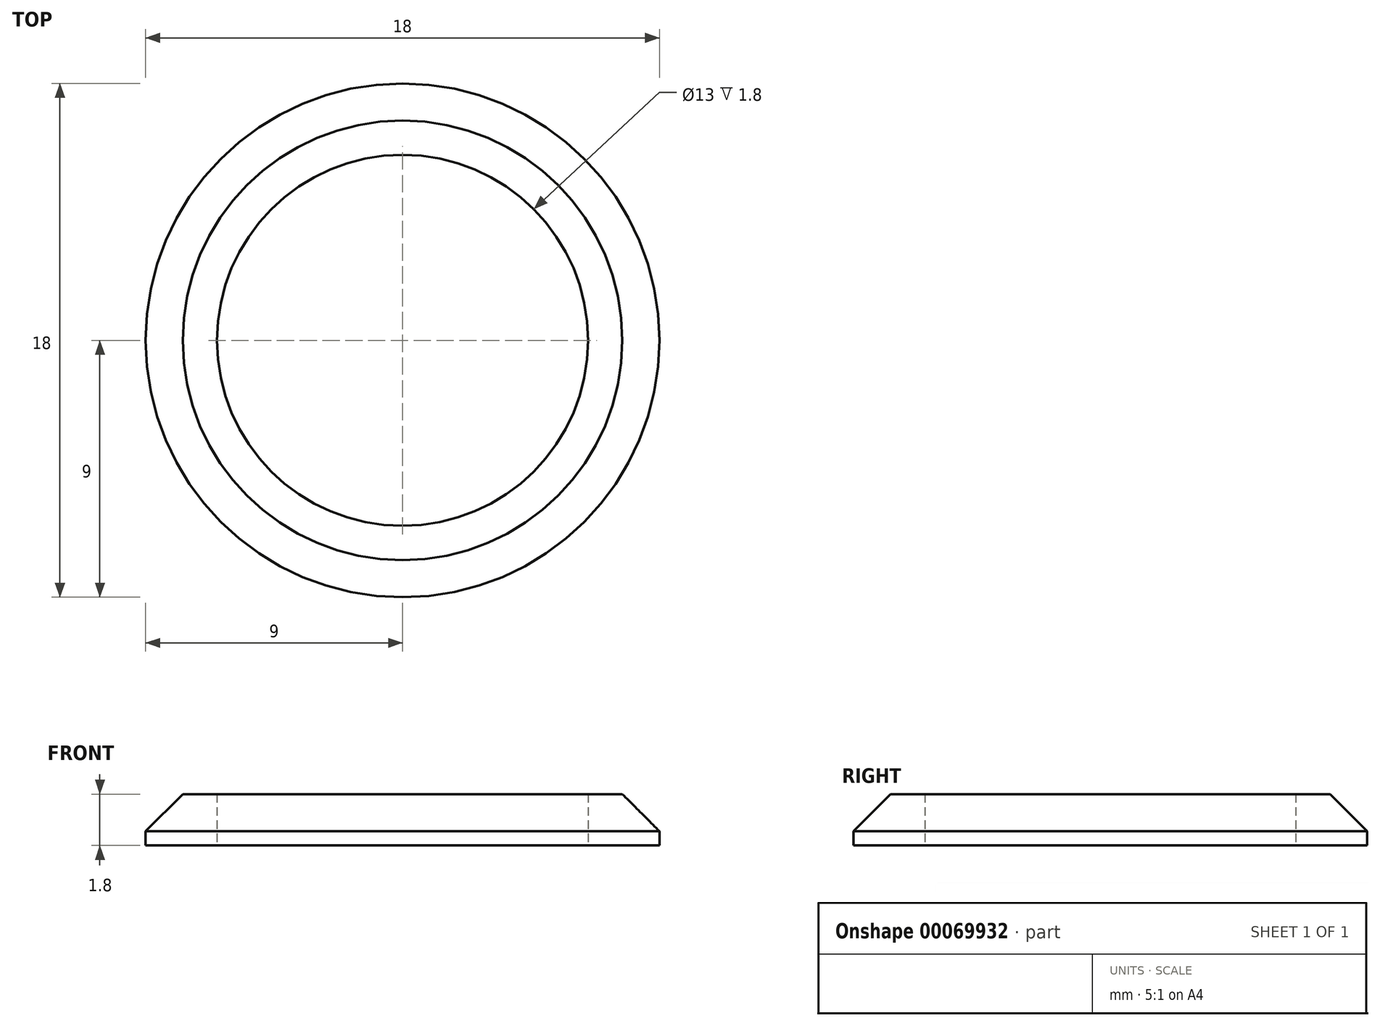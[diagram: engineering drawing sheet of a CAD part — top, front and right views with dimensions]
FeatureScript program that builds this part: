
annotation { "Feature Type Name" : "Feature", "Feature Type Description" : "" }
export const myFeature = defineFeature(function(context is Context, id is Id, definition is map)
    precondition{}
    {
        {
            var Q0;
            Q0=qCreatedBy(makeId("Top.planeOp"),FACE);
            var sketch = newSketch(context, id + "F0", { "sketchPlane" : qUnion([Q0])});
            skCircle(sketch, "E0", {"center": v(0, 0) * mm, "radius": 6.5 * mm});
            skCircle(sketch, "E1", {"center": v(0, 0) * mm, "radius": 9 * mm});
            skSolve(sketch);
        }
        {
            var Q0;
            Q0=makeQuery(id+"F0.imprint","IMPRINT",FACE,{"disambiguationData":[TD([[makeQuery(id+"F0.imprint","IMPRINT",EDGE,{"derivedFrom":sQuery(id+"F0.wireOp",EDGE,"E0")}),-1.0]])]});
            extrude(context, id + "F1", {"entities" : qUnion([Q0]), "depth" : 1.8 * mm});
        }
        {
            var Q0;
            Q0=makeQuery(id+"F1.opExtrude","CAP_EDGE",EDGE,{"disambiguationData":[OSD([sQuery(id+"F0.wireOp",EDGE,"E1")])],"isStart":false});
            chamfer(context, id + "F2", {"entities" : qUnion([Q0]), "width" : 1.3 * mm, "tangentPropagation" : true});
        }
    });
